# Revit family: lgh-n15_25dc_50Hz
name_source: partatom
category: 機械設備
units: mm (PartAtom-declared; Revit-internal decimal feet)

## family parameters
OmniClass タイトル = Heat Exchangers for Ventilation Air
OmniClass 番号 = 23.75.10.34.21
パーツ タイプ = 標準
ロード時にボイドで切り取り = いいえ
丸型コネクタ寸法 = 直径を使用
作業面ベース = いいえ
共有 = いいえ
常に垂直 = はい
部屋計算ポイント = はい

## types (3) — shared parameters
IfcExportAs = IfcAirToAirHeatRecoveryType
IfcExportType = ROTARYWHEEL
MAX静圧 = 0.0 Pa
MIN静圧 = 0.0 Pa
OmniClassCode = 23-27 23 19 11
Panel_Height = 23  [stored 0.0754593 ft]
URL = https://www.mitsubishielectric.co.jp
Uniclass2015Code = Pr_60_60_36_88
Uniclass2015Title = Thermal wheels
Uniclass2015Version = Systems v1.9
パネルマテリアル = 樹脂成形
仕様書バージョン = Version1.0
企業コード = 108420
分類コード = 50052504100080
初期抵抗 = 0.0 Pa
周波数 = 50 Hz
呼称 = 全熱交換ユニット
外気量 = 0.0 m³/h
天吊金具_幅 = 30  [stored 0.0984252 ft]
天吊金具_径 = 7  [stored 0.0229659 ft]
天吊金具_高さ = 10  [stored 0.0328084 ft]
実風量 = 0.0 m³/h
形式 = カセット形
排気量 = 0.0 m³/h
本体マテリアル = 溶融亜鉛めっき鋼板
極数 = 1
構成部品 = パネル
機外静圧 = 0.0 Pa
機外静圧_排気 = 0.0 Pa
法定耐用年数 = 15
温度交換効率 = 60.00%
相 = 1
積算_科目 = 1 空気調和設備
符号 = HEU
製品リリース年月 = 2013/7/1
製品出荷対象 = 国内
製造元 = MITSIBISHI ELECTRIC
設置方法 = カセット形
設計風量 = 0.0 m³/h
説明 = 業務用ロスナイ パワー脱臭カセット形
負荷分類 = 3_ファン類
運転質量 = 0.00 kg
電動機出力 = 0 W
電圧 = 100 V
zero-valued in all types: EAサイズ_W, OAサイズ_W, RAサイズ_D, SAサイズ_D

## per-type parameters (varying)
- LGH-N10DC: Depth=430  [stored 1.41076 ft]; Duct_Depth=60  [stored 0.19685 ft]; Duct_Height=145  [stored 0.475722 ft]; Duct_Pitch=320  [stored 1.04987 ft]; Duct_W=123  [stored 0.403543 ft]; EAサイズ_D=98; Height=318  [stored 1.04331 ft]; MAX風量=100.0 m³/h; MIN風量=60.0 m³/h; OAサイズ_D=98; Panel_Center=0  [stored 0 ft]; Panel_Depth=506  [stored 1.6601 ft]; Panel_Width=763; Width=690  [stored 2.26378 ft]; エンタルピ交換効率_冷房=41.00%; エンタルピ交換効率_暖房=48.00%; 価格=120000 $; 天吊金具ピッチ1=736  [stored 2.4147 ft]; 天吊金具ピッチ2=330; 消費電力=26 W; 製品質量=15.00 kg; 質量=18.00 kg; 面風速=3.5 m/s; 風量=100.0 m³/h; 騒音レベル(dB(A))=30
- LGH-N15DC: Depth=430  [stored 1.41076 ft]; Duct_Depth=90  [stored 0.295276 ft]; Duct_Height=145  [stored 0.475722 ft]; Duct_Pitch=405; Duct_W=123  [stored 0.403543 ft]; EAサイズ_D=98; Height=350  [stored 1.14829 ft]; MAX風量=135.0 m³/h; MIN風量=80.0 m³/h; OAサイズ_D=98; Panel_Center=95; Panel_Depth=506  [stored 1.6601 ft]; Panel_Width=763; Width=880  [stored 2.88714 ft]; エンタルピ交換効率_冷房=40.00%; エンタルピ交換効率_暖房=50.00%; 価格=150000 $; 天吊金具ピッチ1=926  [stored 3.03806 ft]; 天吊金具ピッチ2=330; 消費電力=43 W; 製品質量=18.00 kg; 質量=21.60 kg; 面風速=4.8 m/s; 風量=135.0 m³/h; 騒音レベル(dB(A))=31
- LGH-N25DC: Depth=520  [stored 1.70604 ft]; Duct_Depth=60  [stored 0.19685 ft]; Duct_Height=115  [stored 0.377297 ft]; Duct_Pitch=450  [stored 1.47638 ft]; Duct_W=137  [stored 0.449475 ft]; EAサイズ_D=142  [stored 0.465879 ft]; Height=390  [stored 1.27953 ft]; MAX風量=250.0 m³/h; MIN風量=140.0 m³/h; OAサイズ_D=142  [stored 0.465879 ft]; Panel_Center=0  [stored 0 ft]; Panel_Depth=596  [stored 1.95538 ft]; Panel_Width=955  [stored 3.1332 ft]; Width=880  [stored 2.88714 ft]; エンタルピ交換効率_冷房=42.00%; エンタルピ交換効率_暖房=55.00%; 価格=193000 $; 天吊金具ピッチ1=926  [stored 3.03806 ft]; 天吊金具ピッチ2=420  [stored 1.37795 ft]; 消費電力=88 W; 製品質量=25.00 kg; 質量=30.00 kg; 面風速=3.9 m/s; 風量=250.0 m³/h; 騒音レベル(dB(A))=36

note: column(s) folded — value = type name in every type: モデル

note: [stored X ft] marks values corroborated as IEEE doubles in the binary element streams (Revit-internal decimal feet)
